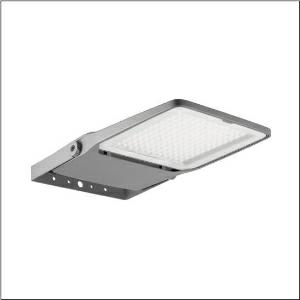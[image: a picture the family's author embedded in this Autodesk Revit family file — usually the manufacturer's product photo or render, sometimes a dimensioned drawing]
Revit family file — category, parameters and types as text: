
# Revit family: floodlight_fl_20_midi___pl52_5xa7682d2d2ac_d313
name_source: partatom
category: Lighting Fixtures
units: mm (PartAtom-declared; Revit-internal decimal feet)

## family parameters
Cut with Voids When Loaded = No
Host = Face
Light Source = No
Part Type = Normal
Room Calculation Point = No
Round Connector Dimension = Use Diameter
Shared = No

## types (1)
- --- (1 x LED 4000K / CRI = 70 (unbekannt), 17990 lm, 4000K)
    Apparent Load = 142 VA
    CIE Flux Codes = 27 59 98 100 100
    Color Rendering = 70
    Color Temperature = 4000K
    Default Elevation = 1800 mm
    Description = Floodlight FL 20 midi, floodlight, primary light control with lens, of plastic, primary optical cover: protective disc, of toughened safety glass, transparent, light distribution: PL52, light emission: direct distribution, primary light characteristic: asymmetric, installation type: surface-mounted, LED High Power LED, rated luminous flux: 17.990 lm, light colour: 740, colour temperature: 4000K, control gear: ECG Plus, control: flexible luminous flux parameterisation, time-dependent luminous flux control, digital communication interface, power reduction, overheat protection, electronic power reduction, with terminal, 5-pole, max. 2.5mm², mains connection: 220..240V, AC, 50/60Hz, rated input power: 142W, LED unit, of diecast aluminium, powder-coated, Siteco® metallic grey (DB 702S), length: 731 mm, width: 450 mm, height: 76mm, housing frame, of diecast aluminium, powder-coated, Siteco® metallic grey (DB 702S), wall fastening, of steel, powder-coated, Siteco® metallic grey (DB 702S), DALIprotection rating (complete): IP66, insulation class (complete): insulation class II (safety insulation), certification: CE, ENEC, VDE, protection symbol: D, permissible ambient temperature for indoor applications: -40..+40°C, permissible ambient temperature for outdoor applications: -40..+50°C, standard: DIN EN 12944, packaging unit: 1 piece

Light Distribution: PL52
    Height = 76 mm
    Lamp = 1 x LED 4000K / CRI >= 70 (unbekannt)
    Lamp Light Flux = 17990 lm
    Lamp count = 1
    Length = 731 mm
    Luminous efficacy = 127 lm/W
    Manufacturer = Siteco
    ModVariant = No
    Model = 5XA7682D2D2AC
    Number of Poles = 1
    OnlyDefault = Yes
    Power Factor = 1
    Product Name = Floodlight FL 20 midi | PL52
    Product group = floodlight | pylon top
    ProductGroupID = 6101
    Protection Class = Protection class II
    Protection Degree = IP 66
    RLX_Detail_Level = 1
    RlxData = <blob elided: 92033 chars, md5=a14ea1b4>
    Socket = socket
    Standby Power = 0 W
    System Light Flux = 17990 lm
    System Power = 142 W
    Type Comments = factory setting: luminous flux: 100 % | dim-lin: 254 | 489 mA
    Type Image = l_1005944.jpg
    URL = http://relux.com
    VarID = @adj_143259
    Voltage = 0 V
    Weight = 0.00 kg
    Width = 450 mm

## geometry (parser evidence)
native form markers: Blend x4, Sweep x15
no freeform markers — native parametric forms only
